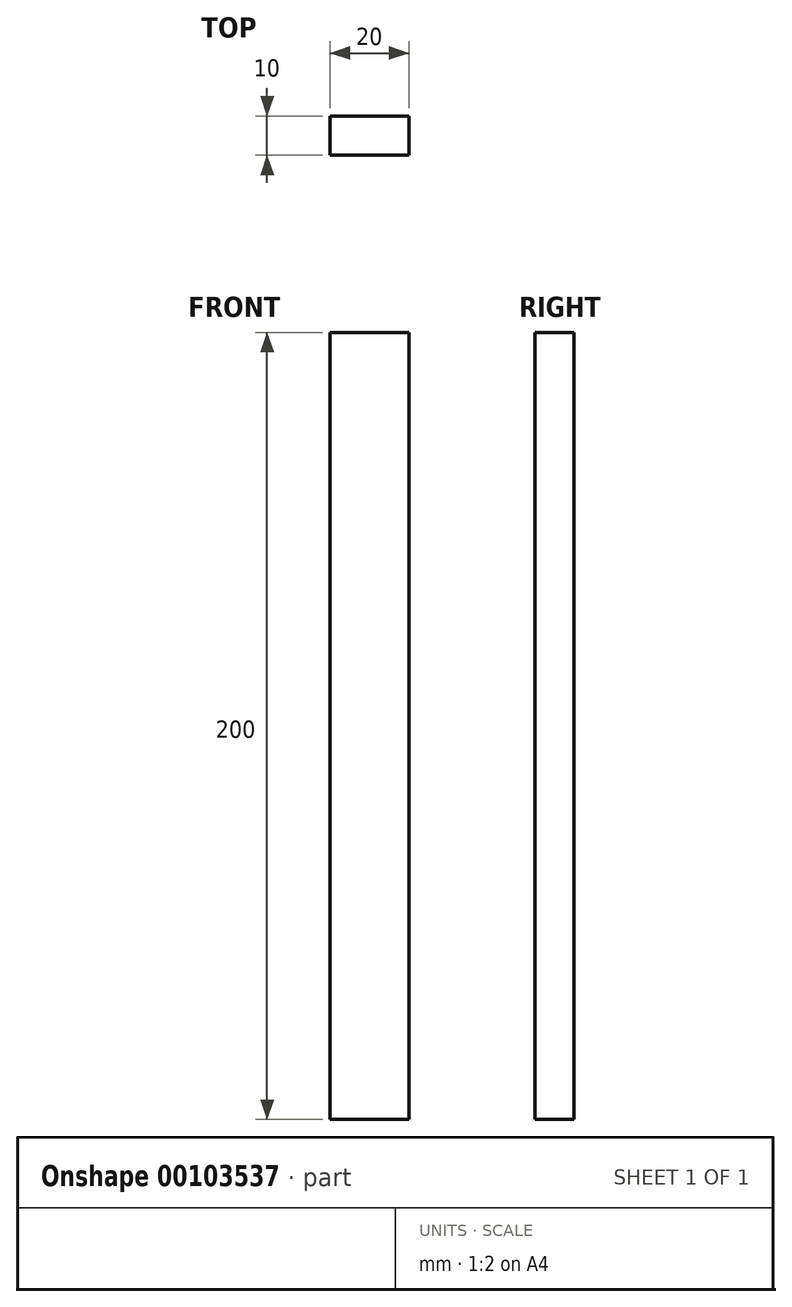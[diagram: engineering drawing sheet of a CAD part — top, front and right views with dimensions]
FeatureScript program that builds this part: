
annotation { "Feature Type Name" : "Feature", "Feature Type Description" : "" }
export const myFeature = defineFeature(function(context is Context, id is Id, definition is map)
    precondition{}
    {
        {
            var Q0;
            Q0=qCreatedBy(makeId("Top.planeOp"),FACE);
            var sketch = newSketch(context, id + "F0", { "sketchPlane" : qUnion([Q0])});
            skLineSegment(sketch, "E0.bottom", {"start": v(29.03, 38.26) * mm, "end": v(49.03, 38.26) * mm});
            skLineSegment(sketch, "E0.top", {"start": v(29.03, 28.26) * mm, "end": v(49.03, 28.26) * mm});
            skLineSegment(sketch, "E0.left", {"start": v(29.03, 38.26) * mm, "end": v(29.03, 28.26) * mm});
            skLineSegment(sketch, "E0.right", {"start": v(49.03, 38.26) * mm, "end": v(49.03, 28.26) * mm});
            skSolve(sketch);
        }
        {
            var Q0;
            Q0=makeQuery(id+"F0.imprint","IMPRINT",FACE,{"disambiguationData":[TD([[makeQuery(id+"F0.imprint","IMPRINT",EDGE,{"derivedFrom":sQuery(id+"F0.wireOp",EDGE,"E0.bottom")}),-1.0]])]});
            extrude(context, id + "F1", {"entities" : qUnion([Q0]), "depth" : 200 * mm});
        }
    });
